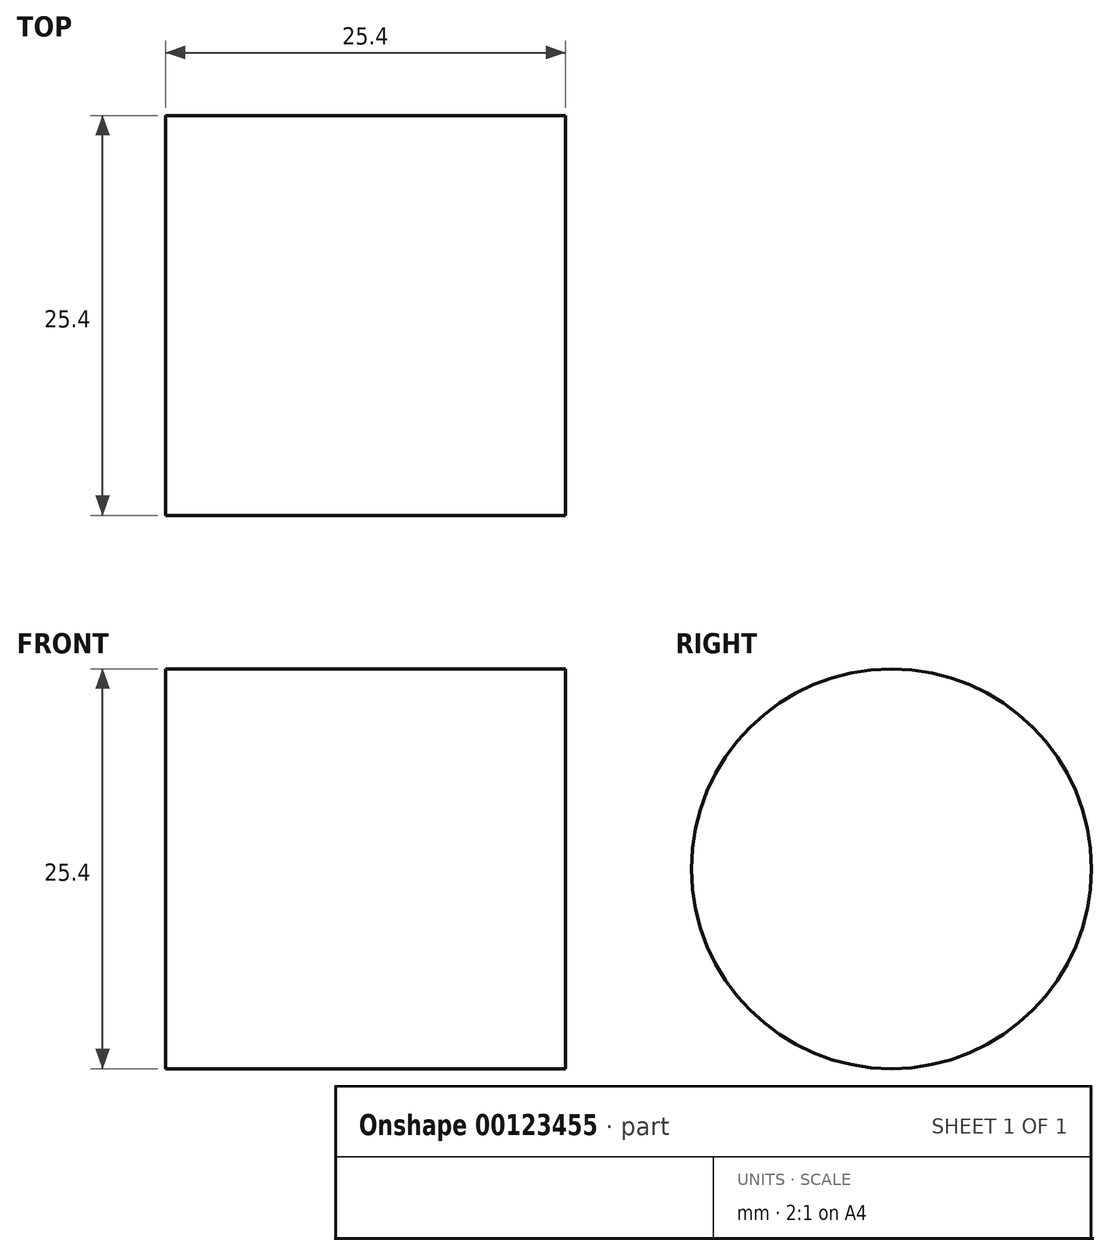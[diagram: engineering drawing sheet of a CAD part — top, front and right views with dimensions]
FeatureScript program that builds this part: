
annotation { "Feature Type Name" : "Feature", "Feature Type Description" : "" }
export const myFeature = defineFeature(function(context is Context, id is Id, definition is map)
    precondition{}
    {
        {
            var Q0;
            Q0=qCreatedBy(makeId("Top.planeOp"),FACE);
            var sketch = newSketch(context, id + "F0", { "sketchPlane" : qUnion([Q0])});
            skLineSegment(sketch, "E0", {"start": v(-25.4, 0) * mm, "end": v(-25.4, 12.7) * mm});
            skLineSegment(sketch, "E1", {"start": v(-25.4, 12.7) * mm, "end": v(0, 12.7) * mm});
            skLineSegment(sketch, "E2", {"start": v(0, 12.7) * mm, "end": v(0, 0) * mm});
            skLineSegment(sketch, "E3", {"start": v(-25.4, 0) * mm, "end": v(0, 0) * mm});
            skSolve(sketch);
        }
        {
            var Q0;
            Q0 = qSketchRegion(id + "F0", true);
            var Q1;
            Q1=sQuery(id+"F0.wireOp",EDGE,"E3");
            revolve(context, id + "F1", {"entities" : qUnion([Q0]), "axis" : qUnion([Q1]), "revolveType" : RevolveType.FULL});
        }
    });
